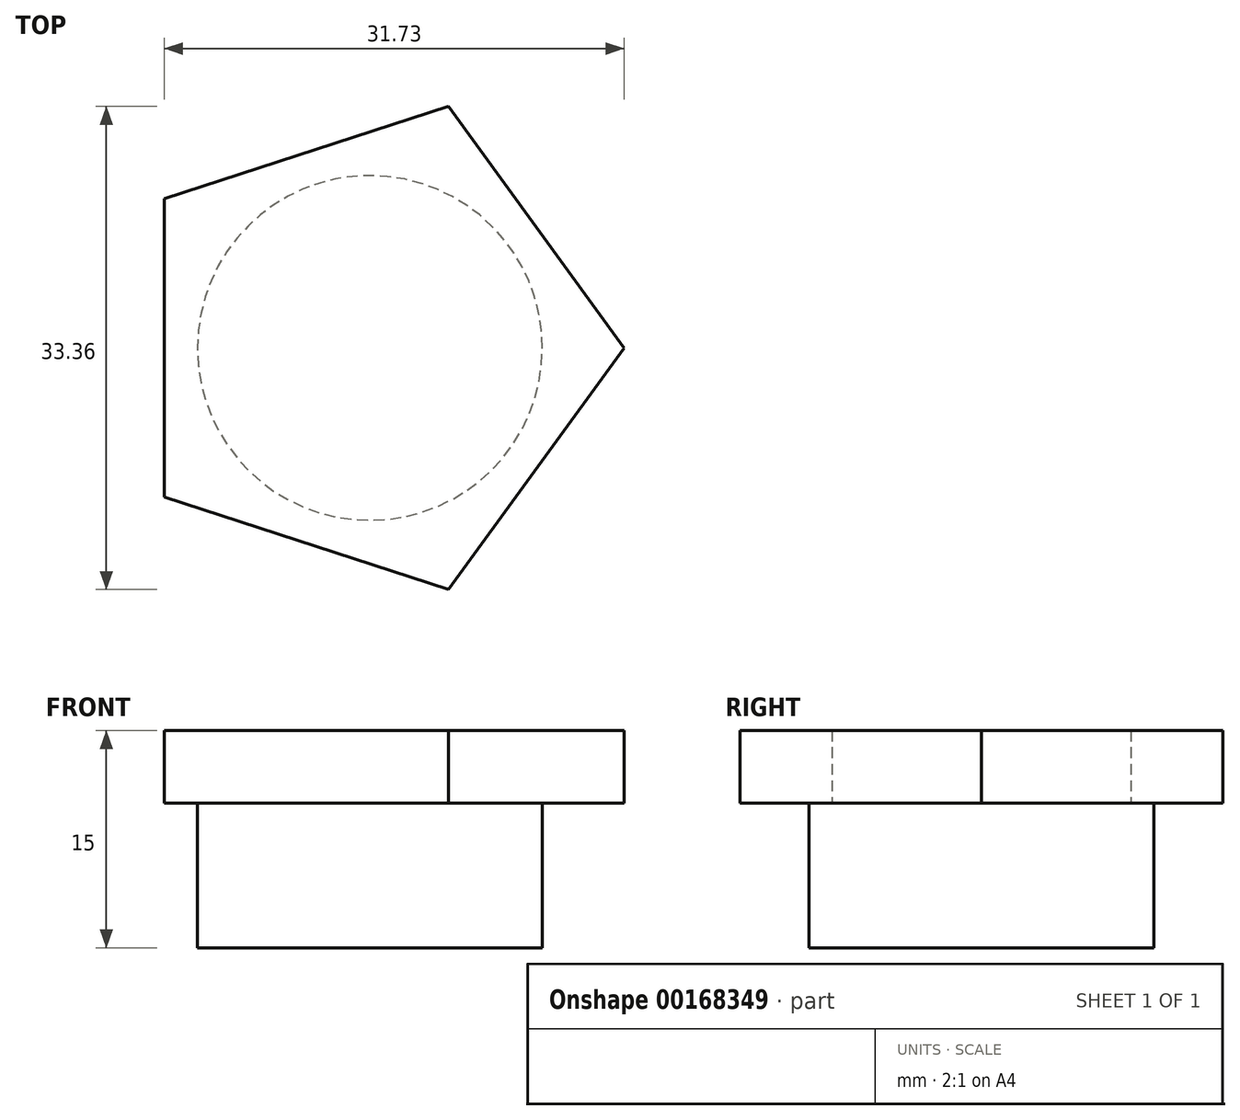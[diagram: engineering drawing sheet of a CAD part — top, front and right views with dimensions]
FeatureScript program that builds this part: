
annotation { "Feature Type Name" : "Feature", "Feature Type Description" : "" }
export const myFeature = defineFeature(function(context is Context, id is Id, definition is map)
    precondition{}
    {
        {
            var Q0;
            Q0=qCreatedBy(makeId("Top.planeOp"),FACE);
            var sketch = newSketch(context, id + "F0", { "sketchPlane" : qUnion([Q0])});
            skCircle(sketch, "E0.cCircle", {"center": v(0, 0) * mm, "radius": 14.19 * mm, "construction": true});
            skLineSegment(sketch, "E0.0", {"start": v(5.42, 16.68) * mm, "end": v(17.54, 0) * mm});
            skLineSegment(sketch, "E0.1", {"start": v(17.54, 0) * mm, "end": v(5.42, -16.68) * mm});
            skLineSegment(sketch, "E0.2", {"start": v(5.42, -16.68) * mm, "end": v(-14.19, -10.3) * mm});
            skLineSegment(sketch, "E0.3", {"start": v(-14.19, -10.3) * mm, "end": v(-14.19, 10.3) * mm});
            skLineSegment(sketch, "E0.4", {"start": v(-14.19, 10.3) * mm, "end": v(5.42, 16.68) * mm});
            skPoint(sketch, "E0.0.midPoint", {"position": v(11.48, 8.34) * mm});
            skSolve(sketch);
        }
        {
            var Q0;
            Q0=qSketchRegion(id+"F0",true);
            extrude(context, id + "F1", {"entities" : qUnion([Q0]), "depth" : 5 * mm});
        }
        {
            var Q0;
            Q0=makeQuery(id+"F1.opExtrude","CAP_FACE",FACE,{"disambiguationData":[OSD([sQuery(id+"F0.wireOp",EDGE,"E0.0"),sQuery(id+"F0.wireOp",EDGE,"E0.1"),sQuery(id+"F0.wireOp",EDGE,"E0.2"),sQuery(id+"F0.wireOp",EDGE,"E0.3"),sQuery(id+"F0.wireOp",EDGE,"E0.4")])],"isStart":false});
            var sketch = newSketch(context, id + "F2", { "sketchPlane" : qUnion([Q0])});
            skCircle(sketch, "E1", {"center": v(0, 0) * mm, "radius": 11.9 * mm});
            skSolve(sketch);
        }
        {
            var Q0;
            Q0=qSketchRegion(id+"F2",true);
            extrude(context, id + "F3", {"entities" : qUnion([Q0]), "operationType" : NewBodyOperationType.ADD, "oppositeDirection" : true, "depth" : 15 * mm});
        }
    });
